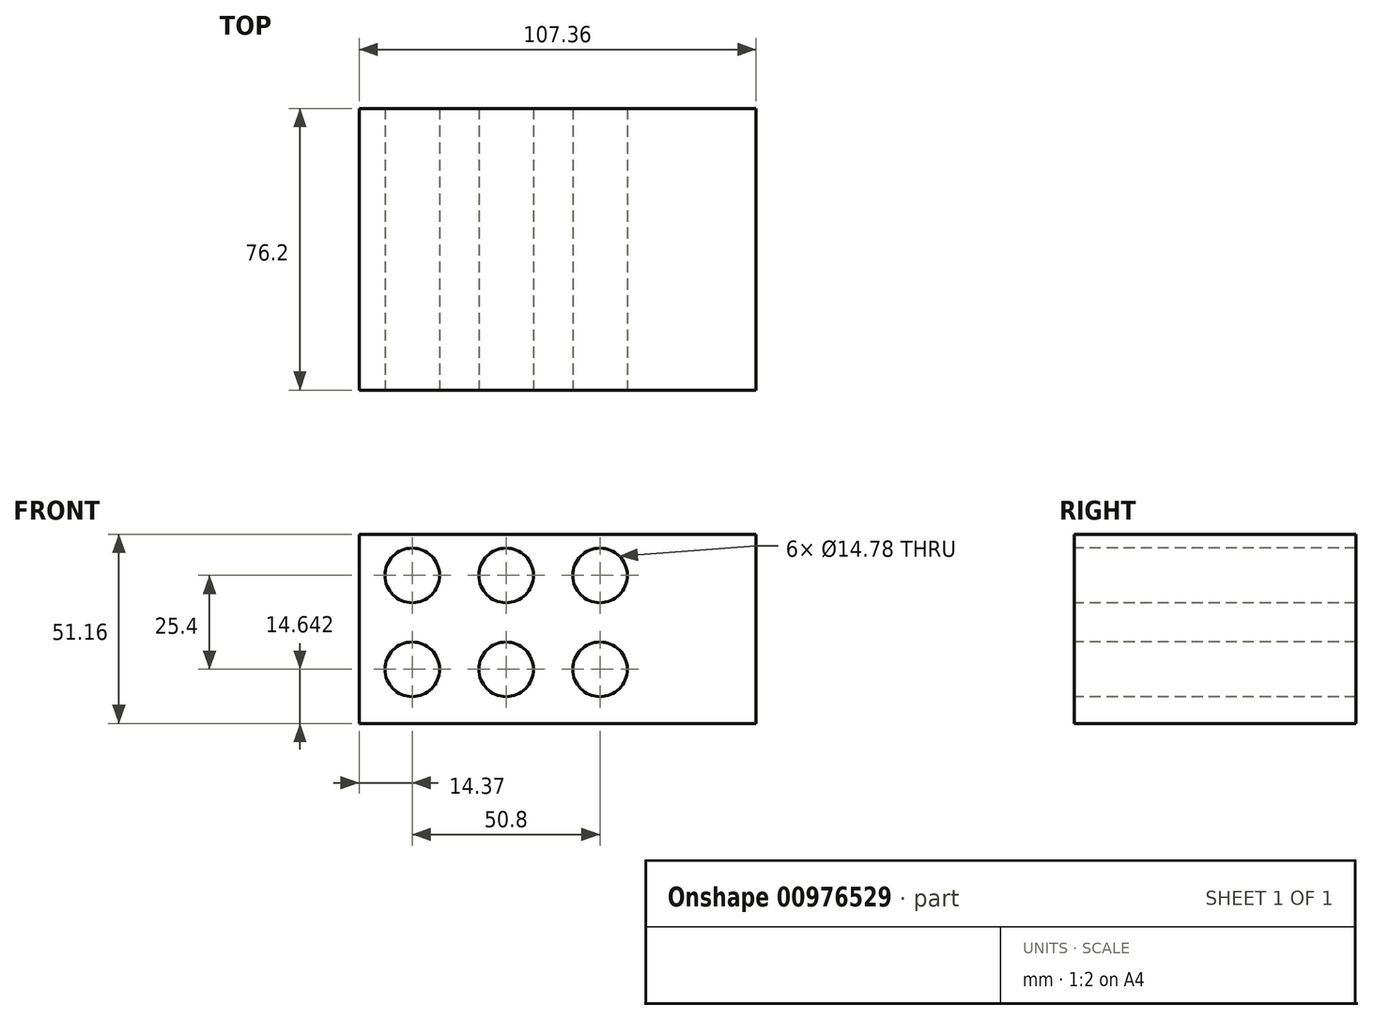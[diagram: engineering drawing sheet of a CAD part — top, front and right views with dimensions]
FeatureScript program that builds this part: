
annotation { "Feature Type Name" : "Feature", "Feature Type Description" : "" }
export const myFeature = defineFeature(function(context is Context, id is Id, definition is map)
    precondition{}
    {
        {
            var Q0;
            Q0=qCreatedBy(makeId("Front.planeOp"),FACE);
            var sketch = newSketch(context, id + "F0", { "sketchPlane" : qUnion([Q0])});
            skLineSegment(sketch, "E0.bottom", {"start": v(-51.7, 26.12) * mm, "end": v(55.66, 26.12) * mm});
            skLineSegment(sketch, "E0.top", {"start": v(-51.7, -25.04) * mm, "end": v(55.66, -25.04) * mm});
            skLineSegment(sketch, "E0.left", {"start": v(-51.7, 26.12) * mm, "end": v(-51.7, -25.04) * mm});
            skLineSegment(sketch, "E0.right", {"start": v(55.66, 26.12) * mm, "end": v(55.66, -25.04) * mm});
            skSolve(sketch);
        }
        {
            var Q0;
            Q0 = qSketchRegion(id + "F0", true);
            extrude(context, id + "F1", {"entities" : qUnion([Q0]), "depth" : 76.2 * mm, "offsetDistance" : 25.4 * mm});
        }
        {
            var Q0;
            Q0=makeQuery(id+"F1.opExtrude","CAP_FACE",FACE,{"disambiguationData":[OSD([sQuery(id+"F0.wireOp",EDGE,"E0.bottom"),sQuery(id+"F0.wireOp",EDGE,"E0.top"),sQuery(id+"F0.wireOp",EDGE,"E0.left"),sQuery(id+"F0.wireOp",EDGE,"E0.right")])],"isStart":false});
            var sketch = newSketch(context, id + "F2", { "sketchPlane" : qUnion([Q0])});
            skSolve(sketch);
        }
        {
            var Q0;
            Q0=makeQuery(id+"F2.imprint","IMPRINT",FACE,{"disambiguationData":[TD([[makeQuery(id+"F2.imprint","IMPRINT",EDGE,{"derivedFrom":makeQuery(id+"F1.opExtrude","CAP_EDGE",EDGE,{"disambiguationData":[OSD([sQuery(id+"F0.wireOp",EDGE,"E0.bottom")])],"isStart":false})}),-1.0]])]});
            var sketch = newSketch(context, id + "F3", { "sketchPlane" : qUnion([Q0])});
            skCircle(sketch, "E1", {"center": v(-37.33, 15) * mm, "radius": 7.39 * mm});
            skCircle(sketch, "E2.0.1.0", {"center": v(-37.33, -10.4) * mm, "radius": 7.39 * mm});
            skCircle(sketch, "E2.1.0.0", {"center": v(-11.93, 15) * mm, "radius": 7.39 * mm});
            skCircle(sketch, "E2.1.1.0", {"center": v(-11.93, -10.4) * mm, "radius": 7.39 * mm});
            skCircle(sketch, "E2.2.0.0", {"center": v(13.47, 15) * mm, "radius": 7.39 * mm});
            skCircle(sketch, "E2.2.1.0", {"center": v(13.47, -10.4) * mm, "radius": 7.39 * mm});
            skLineSegment(sketch, "E2.direction1", {"start": v(-37.33, 15) * mm, "end": v(-11.93, 15) * mm, "construction": true});
            skLineSegment(sketch, "E2.direction2", {"start": v(-37.33, 15) * mm, "end": v(-37.33, -10.4) * mm, "construction": true});
            skSolve(sketch);
        }
        {
            var Q0;
            Q0 = qSketchRegion(id + "F3", true);
            extrude(context, id + "F4", {"entities" : qUnion([Q0]), "operationType" : NewBodyOperationType.REMOVE, "oppositeDirection" : true, "depth" : 84.07 * mm, "offsetDistance" : 25.4 * mm});
        }
    });
